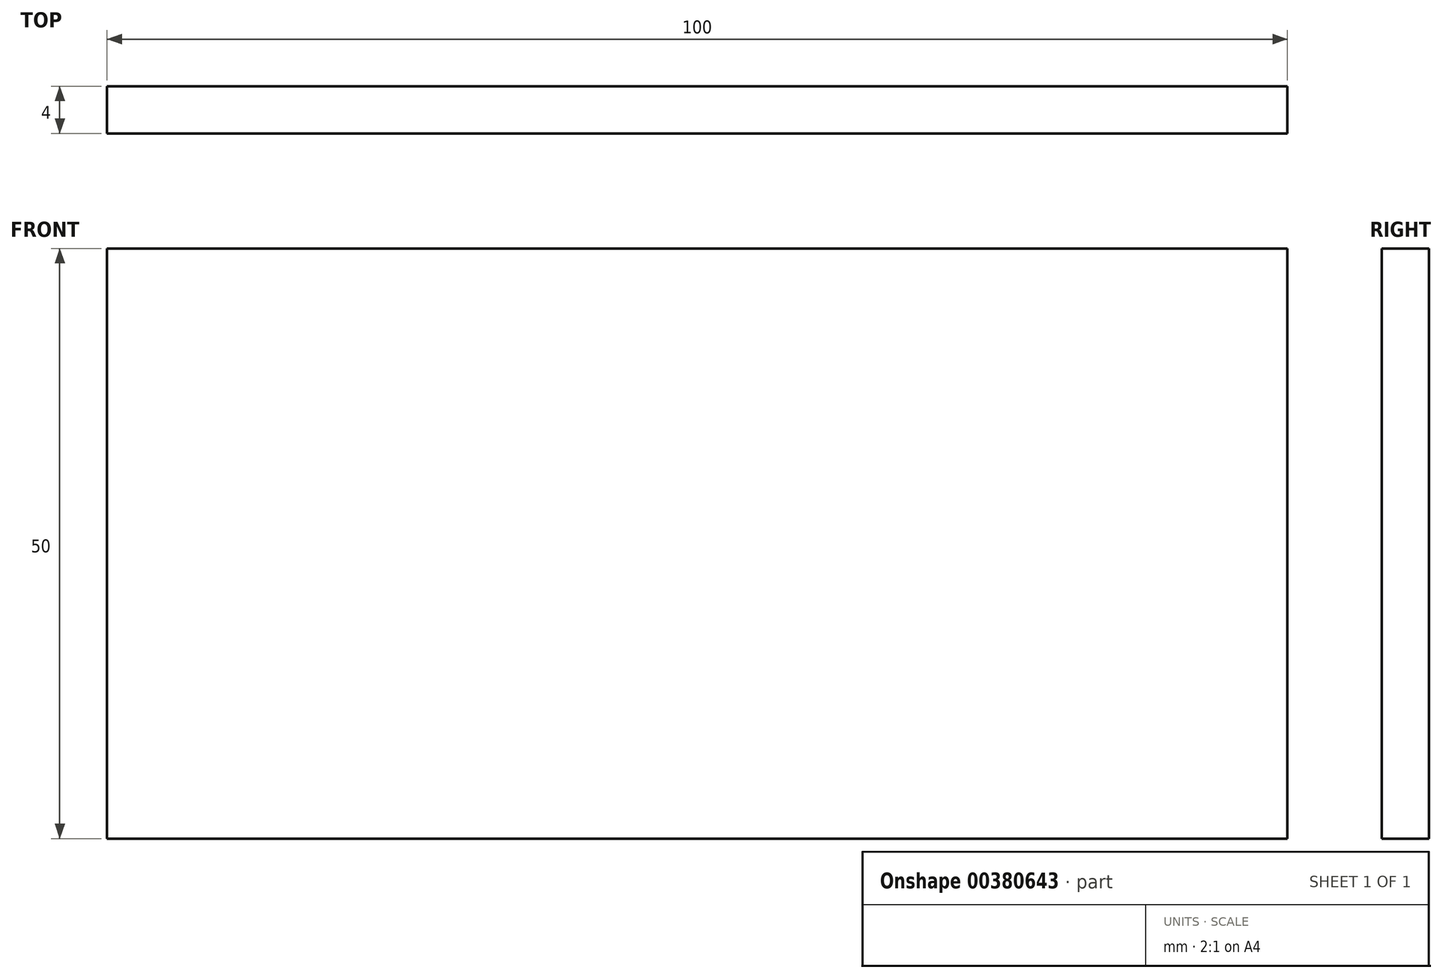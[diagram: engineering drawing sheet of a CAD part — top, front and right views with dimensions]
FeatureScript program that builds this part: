
annotation { "Feature Type Name" : "Feature", "Feature Type Description" : "" }
export const myFeature = defineFeature(function(context is Context, id is Id, definition is map)
    precondition{}
    {
        {
            var Q0;
            Q0=qCreatedBy(makeId("Front.planeOp"),FACE);
            var sketch = newSketch(context, id + "F0", { "sketchPlane" : qUnion([Q0])});
            skLineSegment(sketch, "E0.bottom", {"start": v(-50, 25) * mm, "end": v(50, 25) * mm});
            skLineSegment(sketch, "E0.top", {"start": v(-50, -25) * mm, "end": v(50, -25) * mm});
            skLineSegment(sketch, "E0.left", {"start": v(-50, 25) * mm, "end": v(-50, -25) * mm});
            skLineSegment(sketch, "E0.right", {"start": v(50, 25) * mm, "end": v(50, -25) * mm});
            skSolve(sketch);
        }
        {
            var Q0;
            Q0=makeQuery(id+"F0.imprint","IMPRINT",FACE,{"disambiguationData":[TD([[makeQuery(id+"F0.imprint","IMPRINT",EDGE,{"derivedFrom":sQuery(id+"F0.wireOp",EDGE,"E0.bottom")}),-1.0]])]});
            extrude(context, id + "F1", {"entities" : qUnion([Q0]), "depth" : 4 * mm});
        }
    });
